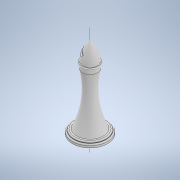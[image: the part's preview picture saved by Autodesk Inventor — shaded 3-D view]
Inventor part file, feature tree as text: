
AUTODESK INVENTOR PART (.ipt)
format: ipt  version: 2022 (Build 260153000, 153)  size: 243,200 bytes
history: native  units: mm
features: other x3, sketch x3, plane x2, extrude x2, revolve x1, fillet x1
ambient origin geometry x8: Origin, YZ Plane, XZ Plane, XY Plane, X Axis, Y Axis, Z Axis, Center Point
bodies: Solid1 (feature_tree)
feature tree (12):
  other  "Back Line Base.ipt"
  revolve  "Revolution1"  [1 undecoded]
  plane  "Work Plane2"
  extrude  "Extrusion1"  Depth=1.0mm
  extrude  "Extrusion2"  Depth=0.5mm
  fillet  "Fillet1"  Radius=12.0mm
  other  "Solid1::Back Line Base.ipt"
  other  "TaggingFeature1"
  sketch  "Sketch1"  dims[d0=10.0mm d1=50.0mm]
  plane  "Work Plane1"
  sketch  "Sketch2"  dims[d2=1.0mm d3=1.0mm]
  sketch  "Sketch3"  dims[d4=1.0mm d5=3.0mm d7=12.0mm d8=1.0mm d9=55.0mm d10=90.0deg d11=17.0mm d12=45.0deg d13=32.5mm d14=2.0mm d15=0.0mm d16=1.0mm d17=2.0mm d18=0.0mm d19=0.5mm]
note: 1 required parameter value undecoded (feature->parameter linkage not recoverable at this tier; creation-order binding heuristic only, values carry confidence <= 0.55)
